# Revit family: Screen-Beam_Mounted-Teknion-JNSABE-Felt_Add-On-R2018
name_source: partatom
category: Furniture
revit_build: Autodesk Revit 2018 (Build: 20190510_1515(x64)
units: mm (PartAtom-declared; Revit-internal decimal feet)

## family parameters
Always vertical = Yes
Cut with Voids When Loaded = No
OmniClass Number = 23.40.20.00
OmniClass Title = General Furniture and Specialties
Room Calculation Point = No
Shared = Yes
Work Plane-Based = No

## types (2) — shared parameters
Assembly Code = E2020200
Manufacturer = Teknion
Manufacturer Fax = 416.661.4586
Part Number = JNSABE
Product Documentation Link = http://www.teknion.com
Product Line = Cityline
Product Page URL = http://www.teknion.com
Series = Cityline
Sustainability Data = http://www.teknion.com
URL = www.teknion.com
Unit Weight URL = http://www.teknion.com
Warranty = http://www.teknion.com

## per-type parameters (varying)
| type | Base Height | Description | Model |
| Standard Height | 27.811 " | Felt Add-On Screen – Beam-Mounted, Standard Height, Radius Corner Detail | JNSABEC___R_ |
| Low Height | 17.626 " | Felt Add-On Screen – Beam-Mounted, Low Height, Radius Corner Detail | JNSABEL___R_ |

## geometry (parser evidence)
native form markers: Sweep x3
no freeform markers — native parametric forms only
